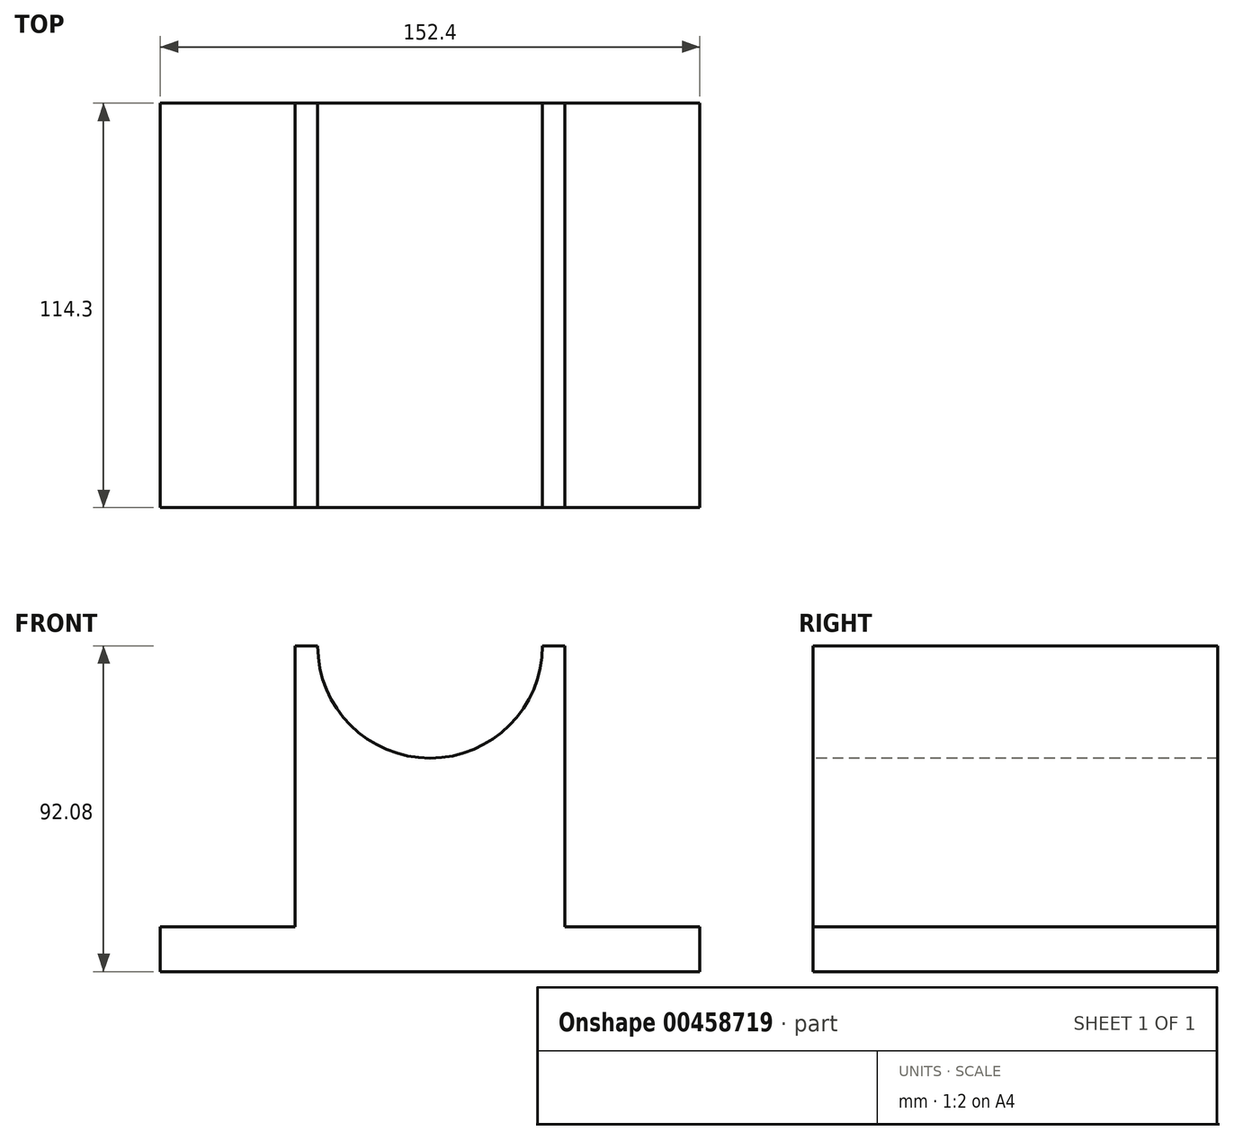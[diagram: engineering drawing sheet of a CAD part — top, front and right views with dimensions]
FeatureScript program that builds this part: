
annotation { "Feature Type Name" : "Feature", "Feature Type Description" : "" }
export const myFeature = defineFeature(function(context is Context, id is Id, definition is map)
    precondition{}
    {
        {
            var Q0;
            Q0=qCreatedBy(makeId("Top.planeOp"),FACE);
            var sketch = newSketch(context, id + "F0", { "sketchPlane" : qUnion([Q0])});
            skLineSegment(sketch, "E0.bottom", {"start": v(76.2, 57.15) * mm, "end": v(-76.2, 57.15) * mm});
            skLineSegment(sketch, "E0.top", {"start": v(76.2, -57.15) * mm, "end": v(-76.2, -57.15) * mm});
            skLineSegment(sketch, "E0.left", {"start": v(76.2, 57.15) * mm, "end": v(76.2, -57.15) * mm});
            skLineSegment(sketch, "E0.right", {"start": v(-76.2, 57.15) * mm, "end": v(-76.2, -57.15) * mm});
            skPoint(sketch, "E0.middle", {"position": v(0, 0) * mm});
            skLineSegment(sketch, "E1", {"start": v(-38.1, 57.15) * mm, "end": v(-38.1, -57.15) * mm});
            skLineSegment(sketch, "E2", {"start": v(38.1, 57.15) * mm, "end": v(38.1, -57.15) * mm});
            skSolve(sketch);
        }
        {
            var Q0;
            {var subQ0=sQuery(id+"F0.wireOp",EDGE,"E0.right");Q0=makeQuery(id+"F0.imprint","IMPRINT",FACE,{"disambiguationData":[TD([[makeQuery(id+"F0.imprint","IMPRINT",EDGE,{"derivedFrom":subQ0}),1.0]])]});}
            var Q1;
            {var subQ0=sQuery(id+"F0.wireOp",EDGE,"E1");Q1=makeQuery(id+"F0.imprint","IMPRINT",FACE,{"disambiguationData":[TD([[makeQuery(id+"F0.imprint","IMPRINT",EDGE,{"derivedFrom":subQ0}),1.0]])]});}
            var Q2;
            {var subQ0=sQuery(id+"F0.wireOp",EDGE,"E0.left");Q2=makeQuery(id+"F0.imprint","IMPRINT",FACE,{"disambiguationData":[TD([[makeQuery(id+"F0.imprint","IMPRINT",EDGE,{"derivedFrom":subQ0}),-1.0]])]});}
            extrude(context, id + "F1", {"entities" : qUnion([Q0, Q1, Q2]), "depth" : 12.7 * mm});
        }
        {
            var Q0;
            {var subQ0=sQuery(id+"F0.wireOp",EDGE,"E1");Q0=makeQuery(id+"F0.imprint","IMPRINT",FACE,{"disambiguationData":[TD([[makeQuery(id+"F0.imprint","IMPRINT",EDGE,{"derivedFrom":subQ0}),1.0]])]});}
            extrude(context, id + "F2", {"entities" : qUnion([Q0]), "operationType" : NewBodyOperationType.ADD, "depth" : 92.07 * mm});
        }
        {
            var Q0;
            {var subQ0=sQuery(id+"F0.wireOp",EDGE,"E0.top");Q0=makeQuery(id+"F2.boolean.opBoolean","MERGE",FACE,{"derivedFrom":[makeQuery(id+"F1.opExtrude","SWEPT_FACE",FACE,{"disambiguationData":[OSD([subQ0])]}),makeQuery(id+"F2.opExtrude","SWEPT_FACE",FACE,{"disambiguationData":[OSD([subQ0])]})]});}
            var sketch = newSketch(context, id + "F3", { "sketchPlane" : qUnion([Q0])});
            skCircle(sketch, "E3", {"center": v(0, 92.08) * mm, "radius": 31.75 * mm});
            skSolve(sketch);
        }
        {
            var Q0;
            Q0 = qSketchRegion(id + "F3", true);
            extrude(context, id + "F4", {"entities" : qUnion([Q0]), "operationType" : NewBodyOperationType.REMOVE, "oppositeDirection" : true, "depth" : 114.3 * mm});
        }
    });
